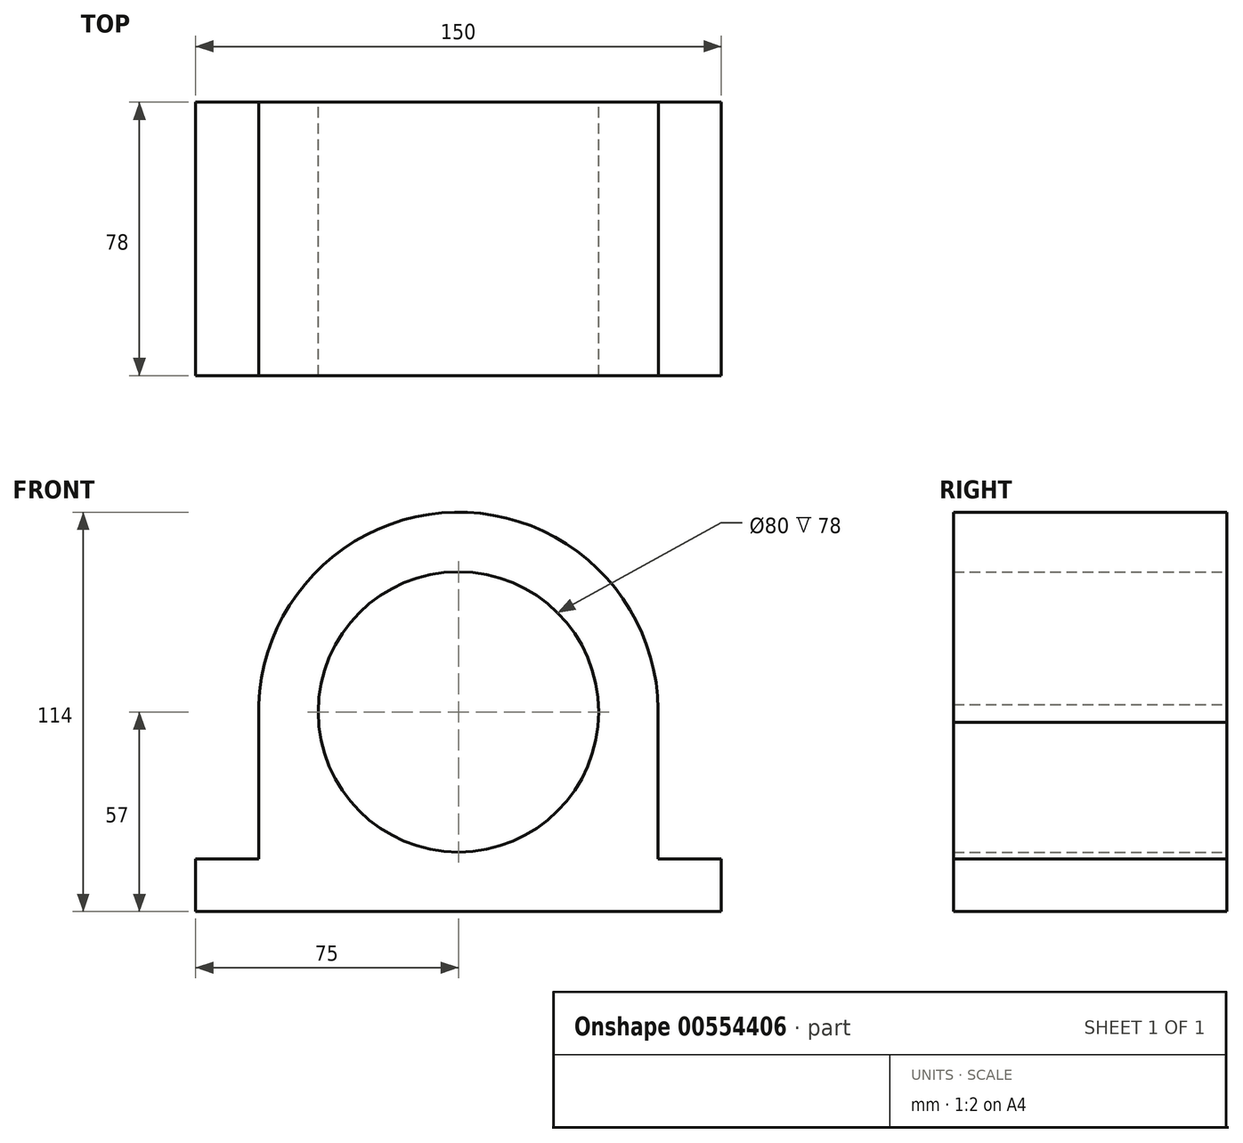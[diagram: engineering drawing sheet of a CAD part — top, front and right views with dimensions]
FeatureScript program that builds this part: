
annotation { "Feature Type Name" : "Feature", "Feature Type Description" : "" }
export const myFeature = defineFeature(function(context is Context, id is Id, definition is map)
    precondition{}
    {
        {
            var Q0;
            Q0=qCreatedBy(makeId("Front.planeOp"),FACE);
            var sketch = newSketch(context, id + "F0", { "sketchPlane" : qUnion([Q0])});
            skLineSegment(sketch, "E0.bottom", {"start": v(0, 0) * mm, "end": v(150, 0) * mm});
            skLineSegment(sketch, "E0.top", {"start": v(0, 15) * mm, "end": v(18.04, 15) * mm});
            skLineSegment(sketch, "E0.left", {"start": v(0, 0) * mm, "end": v(0, 15) * mm});
            skLineSegment(sketch, "E0.right", {"start": v(150, 0) * mm, "end": v(150, 15) * mm});
            skLineSegment(sketch, "E1", {"start": v(75, 15) * mm, "end": v(75, 99) * mm});
            skArc(sketch, "E2", {"start": v(131.92, 53.96) * mm, "mid": v(75.45, 114) * mm, "end": v(18.04, 54.87) * mm});
            skCircle(sketch, "E3", {"center": v(75, 57) * mm, "radius": 40 * mm});
            skLineSegment(sketch, "E4", {"start": v(18.04, 59.13) * mm, "end": v(18.04, 15) * mm});
            skLineSegment(sketch, "E5", {"start": v(131.92, 53.96) * mm, "end": v(131.92, 15) * mm});
            skLineSegment(sketch, "E6.trimOffspring", {"start": v(131.92, 15) * mm, "end": v(150, 15) * mm});
            skSolve(sketch);
        }
        {
            var Q0;
            Q0=makeQuery(id+"F0.imprint","IMPRINT",FACE,{"disambiguationData":[TD([[makeQuery(id+"F0.imprint","IMPRINT",EDGE,{"derivedFrom":sQuery(id+"F0.wireOp",EDGE,"E0.bottom")}),1.0]])]});
            extrude(context, id + "F1", {"entities" : qUnion([Q0]), "depth" : 78 * mm, "offsetDistance" : 25 * mm});
        }
    });
